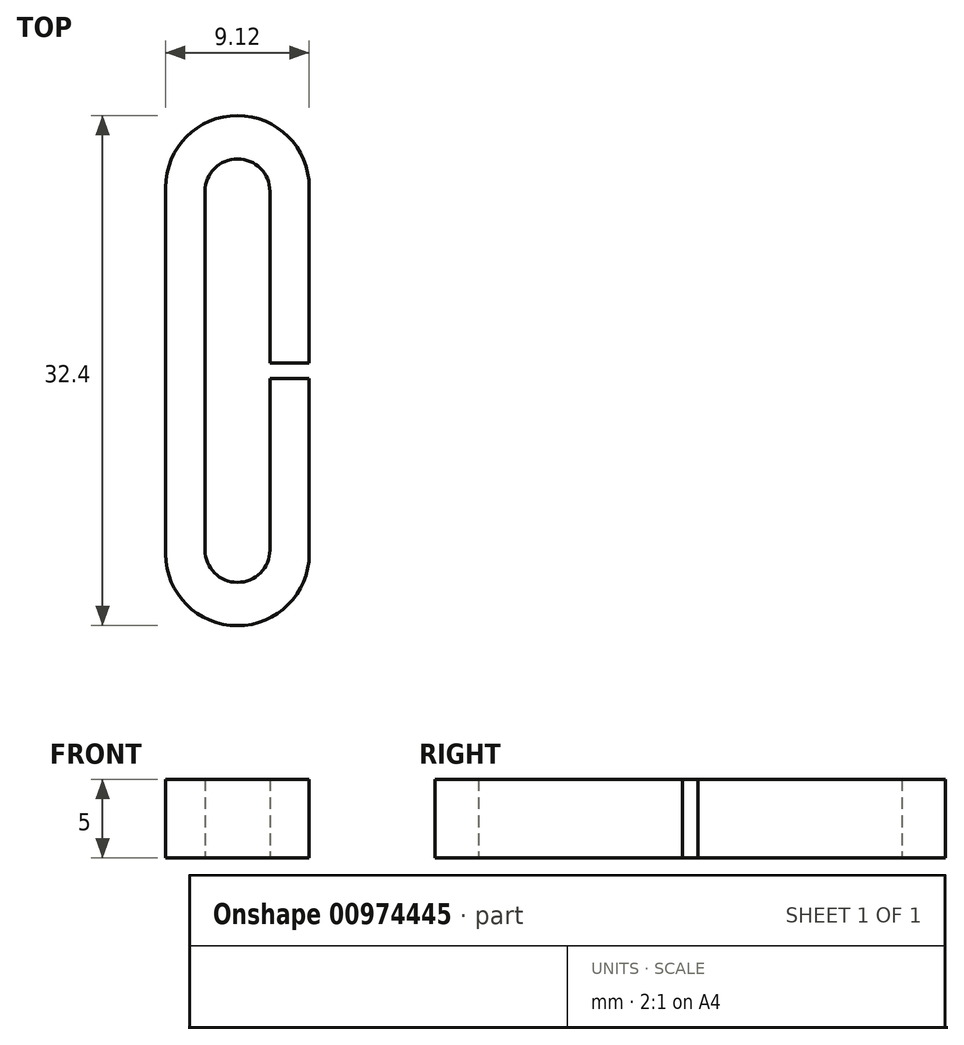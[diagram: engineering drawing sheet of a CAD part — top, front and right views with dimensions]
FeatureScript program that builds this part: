
annotation { "Feature Type Name" : "Feature", "Feature Type Description" : "" }
export const myFeature = defineFeature(function(context is Context, id is Id, definition is map)
    precondition{}
    {
        {
            var Q0;
            Q0=qCreatedBy(makeId("Top.planeOp"),FACE);
            var sketch = newSketch(context, id + "F0", { "sketchPlane" : qUnion([Q0])});
            skLineSegment(sketch, "E0.bottom", {"start": v(4.56, 11.64) * mm, "end": v(-4.56, 11.64) * mm});
            skLineSegment(sketch, "E0.top", {"start": v(4.56, -11.64) * mm, "end": v(-4.56, -11.64) * mm});
            skLineSegment(sketch, "E0.left", {"start": v(4.56, 11.64) * mm, "end": v(4.56, -11.64) * mm});
            skLineSegment(sketch, "E0.right", {"start": v(-4.56, 11.64) * mm, "end": v(-4.56, -11.64) * mm});
            skPoint(sketch, "E0.middle", {"position": v(0, 0) * mm});
            skArc(sketch, "E1", {"start": v(4.56, 11.64) * mm, "mid": v(0, 16.2) * mm, "end": v(-4.56, 11.64) * mm});
            skArc(sketch, "E2", {"start": v(-4.56, -11.64) * mm, "mid": v(0, -16.2) * mm, "end": v(4.56, -11.64) * mm});
            skLineSegment(sketch, "E3.bottom", {"start": v(2.06, 11.4) * mm, "end": v(-2.06, 11.4) * mm});
            skLineSegment(sketch, "E3.top", {"start": v(2.06, -11.4) * mm, "end": v(-2.06, -11.4) * mm});
            skLineSegment(sketch, "E3.left", {"start": v(2.06, 11.4) * mm, "end": v(2.06, -11.4) * mm});
            skLineSegment(sketch, "E3.right", {"start": v(-2.06, 11.4) * mm, "end": v(-2.06, -11.4) * mm});
            skArc(sketch, "E4", {"start": v(2.06, 11.4) * mm, "mid": v(0, 13.45) * mm, "end": v(-2.06, 11.4) * mm});
            skArc(sketch, "E5", {"start": v(-2.06, -11.4) * mm, "mid": v(0, -13.45) * mm, "end": v(2.06, -11.4) * mm});
            skLineSegment(sketch, "E6.bottom", {"start": v(4.56, 0.5) * mm, "end": v(2.05, 0.5) * mm});
            skLineSegment(sketch, "E6.top", {"start": v(4.56, -0.5) * mm, "end": v(2.05, -0.5) * mm});
            skLineSegment(sketch, "E6.left", {"start": v(4.56, 0.5) * mm, "end": v(4.56, -0.5) * mm});
            skLineSegment(sketch, "E6.right", {"start": v(2.05, 0.5) * mm, "end": v(2.05, -0.5) * mm});
            skPoint(sketch, "E6.middle", {"position": v(3.3, 0) * mm});
            skSolve(sketch);
        }
        {
            var Q0;
            {var subQ0=sQuery(id+"F0.wireOp",EDGE,"E1");Q0=makeQuery(id+"F0.imprint","IMPRINT",FACE,{"disambiguationData":[TD([[makeQuery(id+"F0.imprint","IMPRINT",EDGE,{"derivedFrom":subQ0}),1.0]])]});}
            var Q1;
            {var subQ1=sQuery(id+"F0.wireOp",EDGE,"E0.right");Q1=makeQuery(id+"F0.imprint","IMPRINT",FACE,{"disambiguationData":[TD([[makeQuery(id+"F0.imprint","IMPRINT",EDGE,{"derivedFrom":subQ1}),1.0]])]});}
            var Q2;
            {var subQ0=sQuery(id+"F0.wireOp",EDGE,"E2");Q2=makeQuery(id+"F0.imprint","IMPRINT",FACE,{"disambiguationData":[TD([[makeQuery(id+"F0.imprint","IMPRINT",EDGE,{"derivedFrom":subQ0}),1.0]])]});}
            var Q3;
            {var subQ0=sQuery(id+"F0.wireOp",EDGE,"E4");var subQ3=sQuery(id+"F0.wireOp",EDGE,"E0.bottom");var subQ4=makeQuery(id+"F0.imprint","INTERSECT",VERTEX,{"disambiguationData":[OD(0.0)],"derivedFrom":[subQ3,subQ0]});Q3=makeQuery(id+"F0.imprint","IMPRINT",FACE,{"disambiguationData":[TD([[makeQuery(id+"F0.imprint","IMPRINT",EDGE,{"disambiguationData":[TD([[subQ4,1.0]])],"derivedFrom":subQ3}),1.0]])]});}
            var Q4;
            {var subQ0=sQuery(id+"F0.wireOp",EDGE,"E5");var subQ5=sQuery(id+"F0.wireOp",EDGE,"E0.top");var subQ6=makeQuery(id+"F0.imprint","INTERSECT",VERTEX,{"disambiguationData":[OD(0.0)],"derivedFrom":[subQ5,subQ0]});Q4=makeQuery(id+"F0.imprint","IMPRINT",FACE,{"disambiguationData":[TD([[makeQuery(id+"F0.imprint","IMPRINT",EDGE,{"disambiguationData":[TD([[subQ6,1.0]])],"derivedFrom":subQ5}),-1.0]])]});}
            extrude(context, id + "F1", {"entities" : qUnion([Q0, Q1, Q2, Q3, Q4]), "depth" : 5 * mm, "offsetDistance" : 25 * mm});
        }
    });
